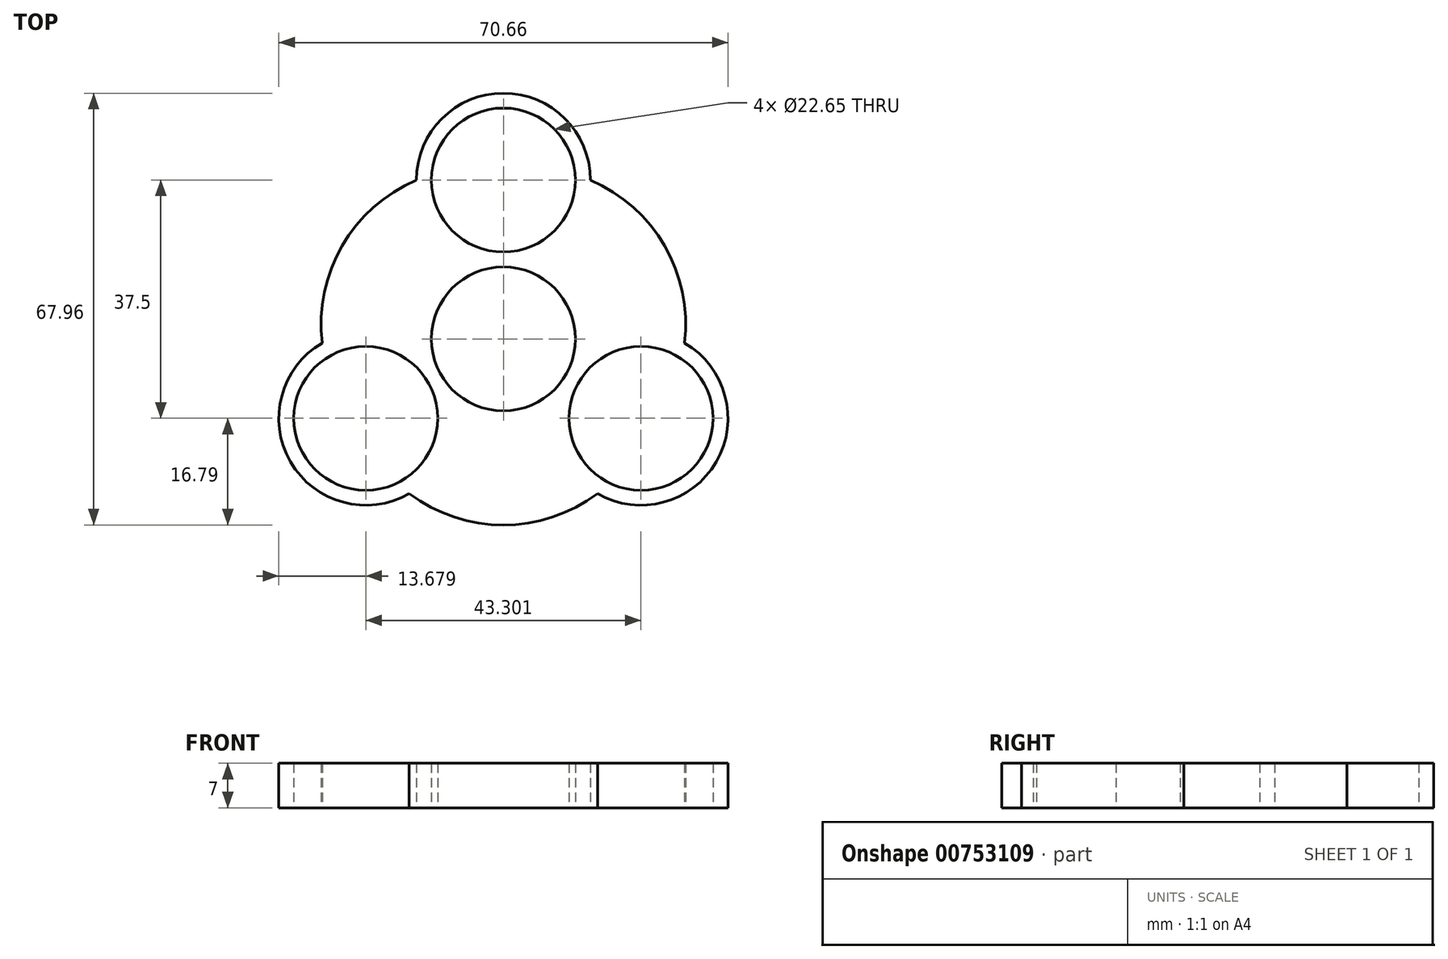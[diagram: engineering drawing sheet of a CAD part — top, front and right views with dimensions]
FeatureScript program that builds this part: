
annotation { "Feature Type Name" : "Feature", "Feature Type Description" : "" }
export const myFeature = defineFeature(function(context is Context, id is Id, definition is map)
    precondition{}
    {
        {
            var Q0;
            Q0=qCreatedBy(makeId("Top.planeOp"),FACE);
            var sketch = newSketch(context, id + "F0", { "sketchPlane" : qUnion([Q0])});
            skCircle(sketch, "E0", {"center": v(0, 0) * mm, "radius": 11.32 * mm});
            skCircle(sketch, "E1", {"center": v(0, 25) * mm, "radius": 11.32 * mm});
            skCircle(sketch, "E2.1.0", {"center": v(-21.65, -12.5) * mm, "radius": 11.32 * mm});
            skArc(sketch, "E2.1.1", {"start": v(-28.49, -0.66) * mm, "mid": v(-33.5, -19.34) * mm, "end": v(-14.81, -24.34) * mm});
            skCircle(sketch, "E2.2.0", {"center": v(21.65, -12.5) * mm, "radius": 11.32 * mm});
            skPoint(sketch, "E3.center", {"position": v(0, 0.27) * mm});
            skArc(sketch, "E4.trimOffspring", {"start": v(13.68, 25) * mm, "mid": v(0, 38.68) * mm, "end": v(-13.68, 25) * mm});
            skArc(sketch, "E5.trimOffspring", {"start": v(14.81, -24.34) * mm, "mid": v(33.5, -19.34) * mm, "end": v(28.49, -0.66) * mm});
            skArc(sketch, "E6", {"start": v(-13.68, 25) * mm, "mid": v(-25.37, 14.65) * mm, "end": v(-28.49, -0.66) * mm});
            skArc(sketch, "E7", {"start": v(28.49, -0.66) * mm, "mid": v(25.37, 14.65) * mm, "end": v(13.67, 25) * mm});
            skArc(sketch, "E8", {"start": v(-14.81, -24.34) * mm, "mid": v(0, -29.3) * mm, "end": v(14.81, -24.34) * mm});
            skPoint(sketch, "E9", {"position": v(-11.32, 13.68) * mm});
            skPoint(sketch, "E10.1.0", {"position": v(-6.18, -16.65) * mm});
            skPoint(sketch, "E10.2.0", {"position": v(17.5, 2.97) * mm});
            skPoint(sketch, "E11", {"position": v(11.33, 13.67) * mm});
            skPoint(sketch, "E12.1.0", {"position": v(-17.5, 2.97) * mm});
            skPoint(sketch, "E12.2.0", {"position": v(6.18, -16.65) * mm});
            skSolve(sketch);
        }
        {
            var Q0;
            Q0 = qSketchRegion(id + "F0", true);
            extrude(context, id + "F1", {"entities" : qUnion([Q0]), "depth" : 7 * mm, "offsetDistance" : 25 * mm});
        }
    });
